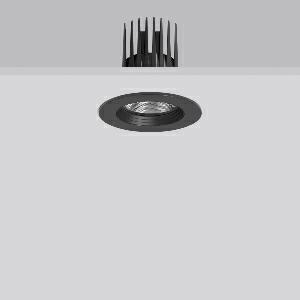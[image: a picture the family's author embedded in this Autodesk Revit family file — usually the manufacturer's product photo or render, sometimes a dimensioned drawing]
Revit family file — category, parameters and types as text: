
# Revit family: heledon_mini_e_901742_003_1_43e1
name_source: partatom
category: Lighting Fixtures
units: mm (PartAtom-declared; Revit-internal decimal feet)

## family parameters
Cut with Voids When Loaded = No
Host = Face
Light Source = No
Part Type = Normal
Room Calculation Point = No
Round Connector Dimension = Use Diameter
Shared = No

## types (1)
- HELEDON mini E (1 x LED Modul 940, 2750 lm, 4000)
    Apparent Load = 20 VA
    Approval mark = CE
    CIE Flux Codes = 95 99 100 100 100
    Color Rendering = 92
    Color Temperature = 4000
    Default Elevation = 1800 mm
    Description = Series: HELEDON mini
Round recessed downlight. Housing: die-cast aluminium, powder-coated. Black plastic ring and recessed LED to prevent glare from the side. Optical assembly with reflector made of MIRO-Silver with 98% total light reflection for outstanding efficiency - can be changed without tools. Best colour rendering index Ra>90. Suitable for Recessed ceiling mounting. Installation without tools thanks to spring fastening system. Including separate LED converter with connecting cable 600 mm.High quality converter without flickering and stroboscopic effect. Through-wiring box (5 pole) available as accessory. The following accessories can be mounted without use of tools: interchangeable lenses, decorative glasses, honeycomb louvre, clear and frosted diffusers, white interchangeable plastic ring. 
Colour: deep black, matt (RAL 9005)
Diameter: 124 mm
Height: 3 mm
Cut-out diameter: 114 mm
Recess height: 170 mm
Luminaire: recess height: 120 mm
Lamp: LED
Socket: without socket
Colour temperature: 4000K
Colour rendering index (CRI): 92
System power: 20 W
Rated luminous flux: 2750 lm
Luminous efficiency: 138 lm/W
Control gear: Regulated power supply
Protection class: II
Type of protection: IP 20
    Height = 0 mm  [stored 0 ft]
    Lamp = 1 x LED Modul 940
    Lamp Light Flux = 2750 lm
    Lamp count = 1
    Length = 124 mm  [stored 0.406824 ft]
    Lifetime = 50000 h
    Luminous efficacy = 138 lm/W
    Manufacturer = RZB
    ModVariant = No
    Model = 901742.003.1
    Mounting Place = Ceiling
    Mounting Type = Recessed
    Number of Poles = 1
    OnlyDefault = Yes
    Power Factor = 1
    Product Name = HELEDON mini E
    Product group = Recessed downlights
    ProductGroupID = 402
    Protection Class = Protection class II
    Protection Degree = IP 20
    RLX_Detail_Level = 1
    RLX_Emergency_Light_Flux = 0 lm
    RLX_Emergency_Type = 0
    RLX_Emergency_Type_DB = No
    RlxData = <blob elided: 128233 chars, md5=fa6d91df>
    Socket = socket
    Standby Power = 0 W
    System Light Flux = 2750 lm
    System Power = 20 W
    Type Comments = Product without accessories
    Type Image = 901657.003.jpg
    URL = http://relux.com
    VarID = ---
    Voltage = 230 V
    Voltage Range = 220-240 V
    Weight = 0.00 kg
    Width = 0 mm  [stored 0 ft]

note: [stored X ft] marks values corroborated as IEEE doubles in the binary element streams (Revit-internal decimal feet)

## geometry (parser evidence)
native form markers: Blend x4, Sweep x11
no freeform markers — native parametric forms only
